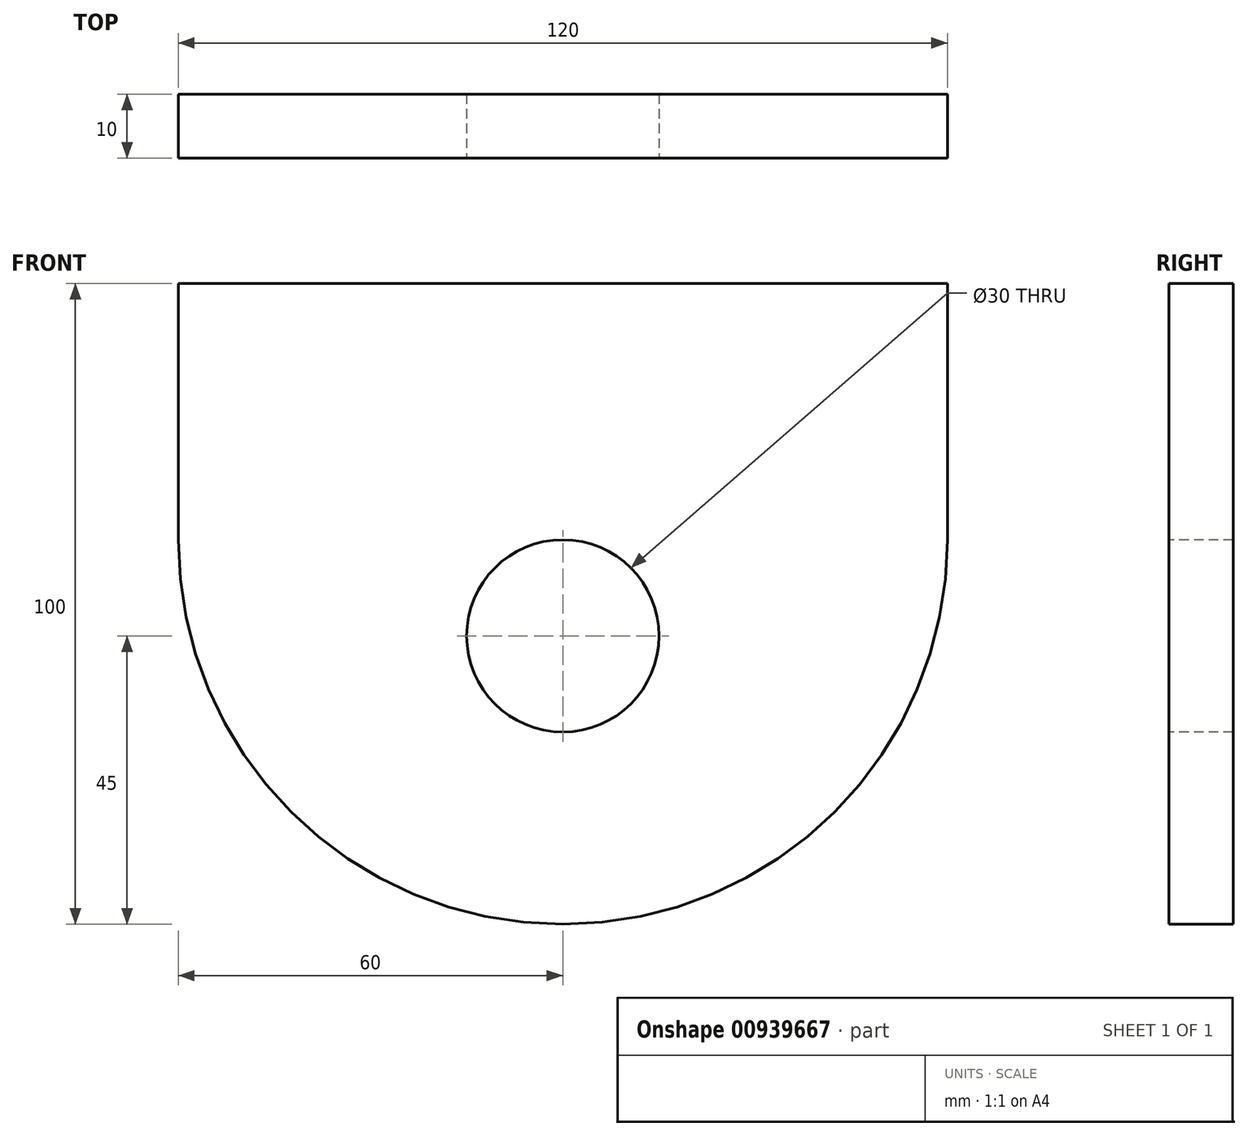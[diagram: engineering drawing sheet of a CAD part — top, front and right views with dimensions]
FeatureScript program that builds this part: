
annotation { "Feature Type Name" : "Feature", "Feature Type Description" : "" }
export const myFeature = defineFeature(function(context is Context, id is Id, definition is map)
    precondition{}
    {
        {
            var Q0;
            Q0=qCreatedBy(makeId("Front.planeOp"),FACE);
            var sketch = newSketch(context, id + "F0", { "sketchPlane" : qUnion([Q0])});
            skLineSegment(sketch, "E0.bottom", {"start": v(60, -50) * mm, "end": v(-60, -50) * mm});
            skLineSegment(sketch, "E0.top", {"start": v(60, 50) * mm, "end": v(-60, 50) * mm});
            skLineSegment(sketch, "E0.left", {"start": v(60, -50) * mm, "end": v(60, 50) * mm});
            skLineSegment(sketch, "E0.right", {"start": v(-60, -50) * mm, "end": v(-60, 50) * mm});
            skPoint(sketch, "E0.middle", {"position": v(0, 0) * mm});
            skSolve(sketch);
        }
        {
            var Q0;
            Q0 = qSketchRegion(id + "F0", true);
            extrude(context, id + "F1", {"entities" : qUnion([Q0]), "oppositeDirection" : true, "depth" : 10 * mm, "offsetDistance" : 25 * mm});
        }
        {
            var Q0;
            Q0=qCreatedBy(makeId("Front.planeOp"),FACE);
            var sketch = newSketch(context, id + "F2", { "sketchPlane" : qUnion([Q0])});
            skCircle(sketch, "E1", {"center": v(0, -5) * mm, "radius": 15 * mm});
            skSolve(sketch);
        }
        {
            var Q0;
            Q0 = qSketchRegion(id + "F2", true);
            extrude(context, id + "F3", {"entities" : qUnion([Q0]), "operationType" : NewBodyOperationType.REMOVE, "endBound" : BoundingType.THROUGH_ALL, "oppositeDirection" : true, "depth" : 25 * mm, "offsetDistance" : 25 * mm});
        }
        {
            var Q0;
            Q0=makeQuery(id+"F1.opExtrude","SWEPT_EDGE",EDGE,{"disambiguationData":[OSD([sQuery(id+"F0.wireOp",EDGE,"E0.bottom"),sQuery(id+"F0.wireOp",EDGE,"E0.right")])]});
            var Q1;
            Q1=makeQuery(id+"F1.opExtrude","SWEPT_EDGE",EDGE,{"disambiguationData":[OSD([sQuery(id+"F0.wireOp",EDGE,"E0.bottom"),sQuery(id+"F0.wireOp",EDGE,"E0.left")])]});
            fillet(context, id + "F4", {"entities" : qUnion([Q0, Q1]), "radius" : 60 * mm, "tangentPropagation" : true, "allowEdgeOverflow" : false});
        }
    });
